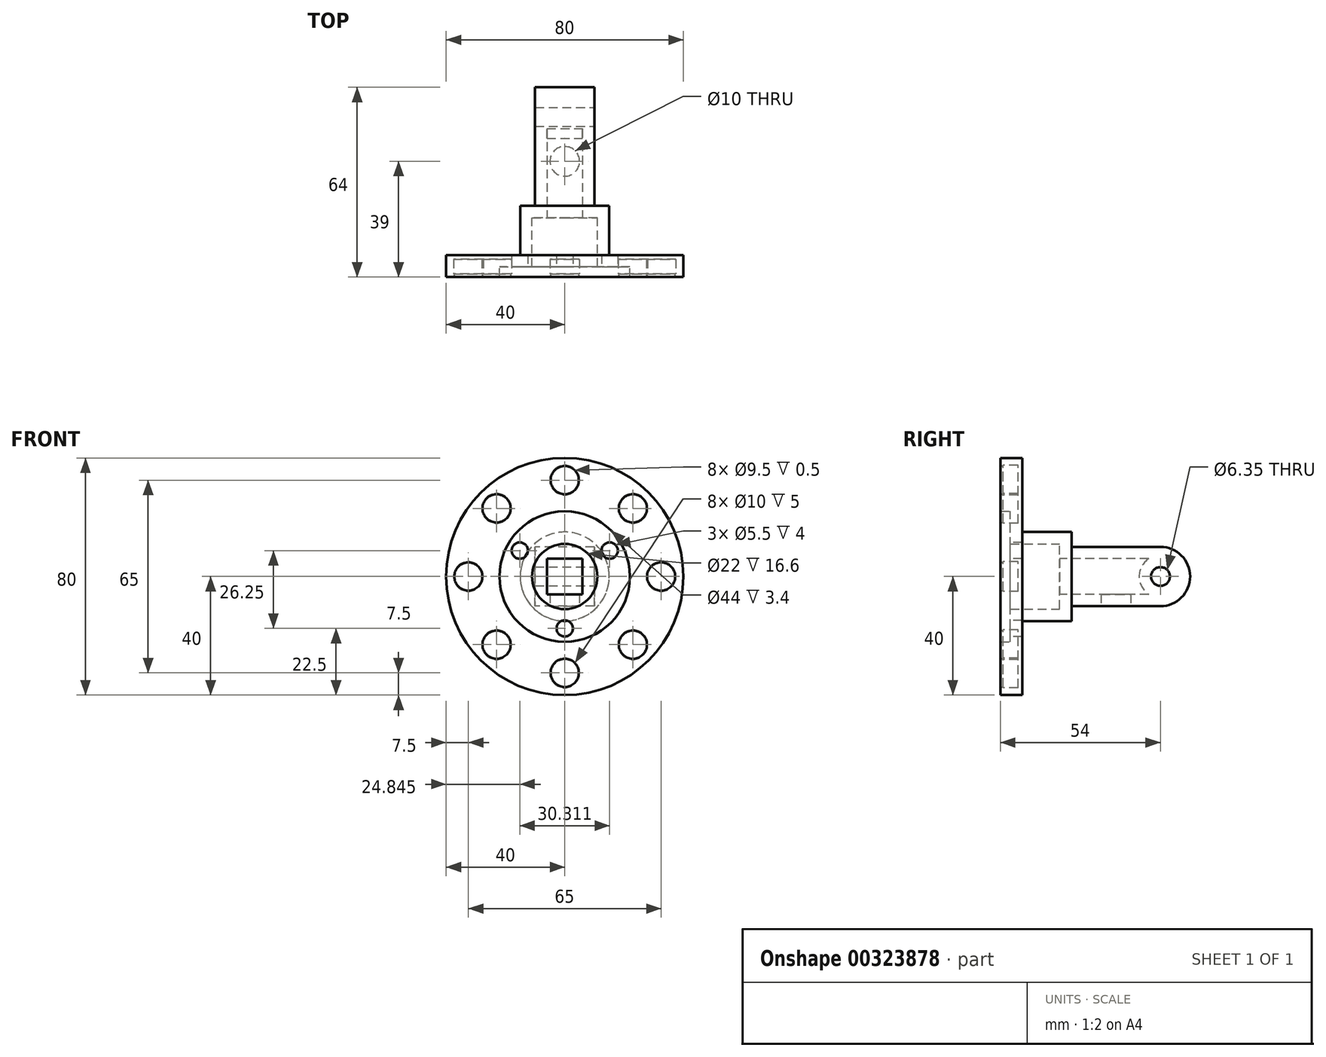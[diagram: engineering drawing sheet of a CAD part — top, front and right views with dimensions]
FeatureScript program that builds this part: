
annotation { "Feature Type Name" : "Feature", "Feature Type Description" : "" }
export const myFeature = defineFeature(function(context is Context, id is Id, definition is map)
    precondition{}
    {
        {
            var Q0;
            Q0=qCreatedBy(makeId("Top.planeOp"),FACE);
            var sketch = newSketch(context, id + "F0", { "sketchPlane" : qUnion([Q0])});
            skLineSegment(sketch, "E0.bottom", {"start": v(10, 15) * mm, "end": v(-10, 15) * mm});
            skLineSegment(sketch, "E0.top", {"start": v(10, -15) * mm, "end": v(-10, -15) * mm});
            skLineSegment(sketch, "E0.left", {"start": v(10, 15) * mm, "end": v(10, -15) * mm});
            skLineSegment(sketch, "E0.right", {"start": v(-10, 15) * mm, "end": v(-10, -15) * mm});
            skPoint(sketch, "E0.middle", {"position": v(0, 0) * mm});
            skSolve(sketch);
        }
        {
            var Q0;
            Q0=makeQuery(id+"F0.imprint","IMPRINT",FACE,{"disambiguationData":[TD([[makeQuery(id+"F0.imprint","IMPRINT",EDGE,{"derivedFrom":sQuery(id+"F0.wireOp",EDGE,"E0.bottom")}),1.0]])]});
            extrude(context, id + "F1", {"entities" : qUnion([Q0]), "depth" : 20 * mm});
        }
        {
            var Q0;
            Q0=makeQuery(id+"F1.opExtrude","CAP_EDGE",EDGE,{"disambiguationData":[OSD([sQuery(id+"F0.wireOp",EDGE,"E0.bottom")])],"isStart":false});
            var Q1;
            Q1=makeQuery(id+"F1.opExtrude","CAP_EDGE",EDGE,{"disambiguationData":[OSD([sQuery(id+"F0.wireOp",EDGE,"E0.bottom")])],"isStart":true});
            fillet(context, id + "F2", {"entities" : qUnion([Q0, Q1]), "radius" : 10 * mm, "tangentPropagation" : true, "allowEdgeOverflow" : false});
        }
        {
            var Q0;
            Q0=makeQuery(id+"F1.opExtrude","SWEPT_FACE",FACE,{"disambiguationData":[OSD([sQuery(id+"F0.wireOp",EDGE,"E0.left")])]});
            var sketch = newSketch(context, id + "F3", { "sketchPlane" : qUnion([Q0])});
            skCircle(sketch, "E1", {"center": v(5, 10) * mm, "radius": 3.18 * mm});
            skSolve(sketch);
        }
        {
            var Q0;
            Q0=makeQuery(id+"F3.imprint","IMPRINT",FACE,{"disambiguationData":[TD([[makeQuery(id+"F3.imprint","IMPRINT",EDGE,{"derivedFrom":sQuery(id+"F3.wireOp",EDGE,"E1")}),1.0]])]});
            extrude(context, id + "F4", {"entities" : qUnion([Q0]), "operationType" : NewBodyOperationType.REMOVE, "oppositeDirection" : true, "depth" : 25 * mm});
        }
        {
            var Q0;
            Q0=makeQuery(id+"F1.opExtrude","SWEPT_FACE",FACE,{"disambiguationData":[OSD([sQuery(id+"F0.wireOp",EDGE,"E0.top")])]});
            extrude(context, id + "F5", {"entities" : qUnion([Q0]), "operationType" : NewBodyOperationType.ADD, "depth" : 10 * mm});
        }
        {
            var Q0;
            Q0=makeQuery(id+"F5.opExtrude","CAP_FACE",FACE,{"disambiguationData":[OSD([sQuery(id+"F0.wireOp",EDGE,"E0.top")])],"isStart":false});
            shell(context, id + "F6", {"entities" : qUnion([Q0]), "thickness" : 4 * mm});
        }
        {
            var Q0;
            {var subQ0=sQuery(id+"F0.wireOp",EDGE,"E0.top");Q0=makeQuery(id+"F5.boolean.opBoolean","MERGE",FACE,{"derivedFrom":[makeQuery(id+"F1.opExtrude","CAP_FACE",FACE,{"disambiguationData":[OSD([sQuery(id+"F0.wireOp",EDGE,"E0.bottom"),subQ0,sQuery(id+"F0.wireOp",EDGE,"E0.left"),sQuery(id+"F0.wireOp",EDGE,"E0.right")])],"isStart":true}),makeQuery(id+"F5.opExtrude","SWEPT_FACE",FACE,{"disambiguationData":[OSD([subQ0]),TDD([makeQuery(id+"F1.opExtrude","CAP_EDGE",EDGE,{"disambiguationData":[OSD([subQ0])],"isStart":true})])]})]});}
            var sketch = newSketch(context, id + "F7", { "sketchPlane" : qUnion([Q0])});
            skCircle(sketch, "E2", {"center": v(0, 10) * mm, "radius": 5 * mm});
            skPoint(sketch, "E2.centerSnap0", {"position": v(0, 25) * mm});
            skSolve(sketch);
        }
        {
            var Q0;
            Q0=makeQuery(id+"F7.imprint","IMPRINT",FACE,{"disambiguationData":[TD([[makeQuery(id+"F7.imprint","IMPRINT",EDGE,{"derivedFrom":sQuery(id+"F7.wireOp",EDGE,"E2")}),1.0]])]});
            extrude(context, id + "F8", {"entities" : qUnion([Q0]), "operationType" : NewBodyOperationType.REMOVE, "oppositeDirection" : true, "depth" : 4 * mm});
        }
        {
            var Q0;
            Q0=makeQuery(id+"F5.opExtrude","CAP_FACE",FACE,{"disambiguationData":[OSD([sQuery(id+"F0.wireOp",EDGE,"E0.top")])],"isStart":false});
            var sketch = newSketch(context, id + "F9", { "sketchPlane" : qUnion([Q0])});
            skCircle(sketch, "E3", {"center": v(0, 10) * mm, "radius": 15 * mm});
            skPoint(sketch, "E3.centerSnap0", {"position": v(10, 10) * mm});
            skSolve(sketch);
        }
        {
            var Q0;
            Q0=makeQuery(id+"F9.imprint","IMPRINT",FACE,{"disambiguationData":[TD([[makeQuery(id+"F9.imprint","IMPRINT",EDGE,{"derivedFrom":sQuery(id+"F9.wireOp",EDGE,"E3")}),1.0]])]});
            var Q1;
            {var subQ0=sQuery(id+"F0.wireOp",EDGE,"E0.top");var subQ2=makeQuery(id+"F5.opExtrude","CAP_EDGE",EDGE,{"disambiguationData":[OSD([subQ0]),TDD([makeQuery(id+"F1.opExtrude","CAP_EDGE",EDGE,{"disambiguationData":[OSD([subQ0])],"isStart":true})])],"isStart":false});Q1=makeQuery(id+"F9.imprint","IMPRINT",FACE,{"disambiguationData":[TD([[makeQuery(id+"F9.imprint","IMPRINT",EDGE,{"derivedFrom":subQ2}),-1.0]])]});}
            extrude(context, id + "F10", {"entities" : qUnion([Q0, Q1]), "operationType" : NewBodyOperationType.ADD, "depth" : 4 * mm});
        }
        {
            var Q0;
            Q0=makeQuery(id+"F10.opExtrude","CAP_FACE",FACE,{"disambiguationData":[OSD([sQuery(id+"F0.wireOp",EDGE,"E0.top"),sQuery(id+"F0.wireOp",EDGE,"E0.left"),sQuery(id+"F0.wireOp",EDGE,"E0.right"),sQuery(id+"F9.wireOp",EDGE,"E3")])],"isStart":false});
            var sketch = newSketch(context, id + "F11", { "sketchPlane" : qUnion([Q0])});
            skCircle(sketch, "E4", {"center": v(0, 10) * mm, "radius": 11 * mm});
            skSolve(sketch);
        }
        {
            var Q0;
            Q0=makeQuery(id+"F11.imprint","IMPRINT",FACE,{"disambiguationData":[TD([[makeQuery(id+"F11.imprint","IMPRINT",EDGE,{"derivedFrom":sQuery(id+"F11.wireOp",EDGE,"E4")}),-1.0]])]});
            extrude(context, id + "F12", {"entities" : qUnion([Q0]), "operationType" : NewBodyOperationType.ADD, "depth" : 12.6 * mm});
        }
        {
            var Q0;
            Q0=makeQuery(id+"F12.opExtrude","CAP_FACE",FACE,{"disambiguationData":[OSD([sQuery(id+"F9.wireOp",EDGE,"E3"),sQuery(id+"F11.wireOp",EDGE,"E4")])],"isStart":false});
            var sketch = newSketch(context, id + "F13", { "sketchPlane" : qUnion([Q0])});
            skCircle(sketch, "E5", {"center": v(0, 10) * mm, "radius": 40 * mm});
            skSolve(sketch);
        }
        {
            var Q0;
            Q0=makeQuery(id+"F13.imprint","IMPRINT",FACE,{"disambiguationData":[TD([[makeQuery(id+"F13.imprint","IMPRINT",EDGE,{"derivedFrom":makeQuery(id+"F12.opExtrude","CAP_EDGE",EDGE,{"disambiguationData":[OSD([sQuery(id+"F11.wireOp",EDGE,"E4")])],"isStart":false})}),-1.0]])]});
            var Q1;
            Q1=makeQuery(id+"F13.imprint","IMPRINT",FACE,{"disambiguationData":[TD([[makeQuery(id+"F13.imprint","IMPRINT",EDGE,{"derivedFrom":sQuery(id+"F13.wireOp",EDGE,"E5")}),1.0]])]});
            extrude(context, id + "F14", {"entities" : qUnion([Q0, Q1]), "operationType" : NewBodyOperationType.ADD, "depth" : 4 * mm});
        }
        {
            var Q0;
            Q0=makeQuery(id+"F14.opExtrude","CAP_FACE",FACE,{"disambiguationData":[OSD([sQuery(id+"F11.wireOp",EDGE,"E4"),sQuery(id+"F13.wireOp",EDGE,"E5")])],"isStart":false});
            var sketch = newSketch(context, id + "F15", { "sketchPlane" : qUnion([Q0])});
            skCircle(sketch, "E6", {"center": v(0, 10) * mm, "radius": 22 * mm});
            skSolve(sketch);
        }
        {
            var Q0;
            Q0=makeQuery(id+"F15.imprint","IMPRINT",FACE,{"disambiguationData":[TD([[makeQuery(id+"F15.imprint","IMPRINT",EDGE,{"derivedFrom":sQuery(id+"F15.wireOp",EDGE,"E6")}),-1.0]])]});
            extrude(context, id + "F16", {"entities" : qUnion([Q0]), "operationType" : NewBodyOperationType.ADD, "depth" : 2.4 * mm});
        }
        {
            var Q0;
            Q0=makeQuery(id+"F14.opExtrude","CAP_FACE",FACE,{"disambiguationData":[OSD([sQuery(id+"F11.wireOp",EDGE,"E4"),sQuery(id+"F13.wireOp",EDGE,"E5")])],"isStart":false});
            var sketch = newSketch(context, id + "F17", { "sketchPlane" : qUnion([Q0])});
            skCircle(sketch, "E7", {"center": v(0, -7.5) * mm, "radius": 2.75 * mm});
            skCircle(sketch, "E8.1.0", {"center": v(15.16, 18.75) * mm, "radius": 2.75 * mm});
            skCircle(sketch, "E8.2.0", {"center": v(-15.16, 18.75) * mm, "radius": 2.75 * mm});
            skPoint(sketch, "E8.center", {"position": v(0, 10) * mm});
            skSolve(sketch);
        }
        {
            var Q0;
            Q0=makeQuery(id+"F17.imprint","IMPRINT",FACE,{"disambiguationData":[TD([[makeQuery(id+"F17.imprint","IMPRINT",EDGE,{"derivedFrom":sQuery(id+"F17.wireOp",EDGE,"E8.1.0")}),1.0]])]});
            var Q1;
            Q1=makeQuery(id+"F17.imprint","IMPRINT",FACE,{"disambiguationData":[TD([[makeQuery(id+"F17.imprint","IMPRINT",EDGE,{"derivedFrom":sQuery(id+"F17.wireOp",EDGE,"E7")}),1.0]])]});
            var Q2;
            Q2=makeQuery(id+"F17.imprint","IMPRINT",FACE,{"disambiguationData":[TD([[makeQuery(id+"F17.imprint","IMPRINT",EDGE,{"derivedFrom":sQuery(id+"F17.wireOp",EDGE,"E8.2.0")}),1.0]])]});
            extrude(context, id + "F18", {"entities" : qUnion([Q0, Q1, Q2]), "operationType" : NewBodyOperationType.REMOVE, "oppositeDirection" : true, "depth" : 4 * mm});
        }
        {
            var Q0;
            Q0=makeQuery(id+"F16.opExtrude","CAP_FACE",FACE,{"disambiguationData":[OSD([sQuery(id+"F13.wireOp",EDGE,"E5"),sQuery(id+"F15.wireOp",EDGE,"E6")])],"isStart":false});
            var sketch = newSketch(context, id + "F19", { "sketchPlane" : qUnion([Q0])});
            skCircle(sketch, "E9", {"center": v(0, -22.5) * mm, "radius": 5 * mm});
            skCircle(sketch, "E10.1.0", {"center": v(22.98, -12.98) * mm, "radius": 5 * mm});
            skCircle(sketch, "E10.2.0", {"center": v(32.5, 10) * mm, "radius": 5 * mm});
            skCircle(sketch, "E10.3.0", {"center": v(22.98, 32.98) * mm, "radius": 5 * mm});
            skCircle(sketch, "E10.4.0", {"center": v(0, 42.5) * mm, "radius": 5 * mm});
            skCircle(sketch, "E10.5.0", {"center": v(-22.98, 32.98) * mm, "radius": 5 * mm});
            skCircle(sketch, "E10.6.0", {"center": v(-32.5, 10) * mm, "radius": 5 * mm});
            skCircle(sketch, "E10.7.0", {"center": v(-22.98, -12.98) * mm, "radius": 5 * mm});
            skPoint(sketch, "E10.center", {"position": v(0, 10) * mm});
            skSolve(sketch);
        }
        {
            var Q0;
            Q0=makeQuery(id+"F19.imprint","IMPRINT",FACE,{"disambiguationData":[TD([[makeQuery(id+"F19.imprint","IMPRINT",EDGE,{"derivedFrom":sQuery(id+"F19.wireOp",EDGE,"E10.4.0")}),1.0]])]});
            var Q1;
            Q1=makeQuery(id+"F19.imprint","IMPRINT",FACE,{"disambiguationData":[TD([[makeQuery(id+"F19.imprint","IMPRINT",EDGE,{"derivedFrom":sQuery(id+"F19.wireOp",EDGE,"E10.5.0")}),1.0]])]});
            var Q2;
            Q2=makeQuery(id+"F19.imprint","IMPRINT",FACE,{"disambiguationData":[TD([[makeQuery(id+"F19.imprint","IMPRINT",EDGE,{"derivedFrom":sQuery(id+"F19.wireOp",EDGE,"E10.6.0")}),1.0]])]});
            var Q3;
            Q3=makeQuery(id+"F19.imprint","IMPRINT",FACE,{"disambiguationData":[TD([[makeQuery(id+"F19.imprint","IMPRINT",EDGE,{"derivedFrom":sQuery(id+"F19.wireOp",EDGE,"E10.7.0")}),1.0]])]});
            var Q4;
            Q4=makeQuery(id+"F19.imprint","IMPRINT",FACE,{"disambiguationData":[TD([[makeQuery(id+"F19.imprint","IMPRINT",EDGE,{"derivedFrom":sQuery(id+"F19.wireOp",EDGE,"E9")}),1.0]])]});
            var Q5;
            Q5=makeQuery(id+"F19.imprint","IMPRINT",FACE,{"disambiguationData":[TD([[makeQuery(id+"F19.imprint","IMPRINT",EDGE,{"derivedFrom":sQuery(id+"F19.wireOp",EDGE,"E10.1.0")}),1.0]])]});
            var Q6;
            Q6=makeQuery(id+"F19.imprint","IMPRINT",FACE,{"disambiguationData":[TD([[makeQuery(id+"F19.imprint","IMPRINT",EDGE,{"derivedFrom":sQuery(id+"F19.wireOp",EDGE,"E10.2.0")}),1.0]])]});
            var Q7;
            Q7=makeQuery(id+"F19.imprint","IMPRINT",FACE,{"disambiguationData":[TD([[makeQuery(id+"F19.imprint","IMPRINT",EDGE,{"derivedFrom":sQuery(id+"F19.wireOp",EDGE,"E10.3.0")}),1.0]])]});
            extrude(context, id + "F20", {"entities" : qUnion([Q0, Q1, Q2, Q3, Q4, Q5, Q6, Q7]), "operationType" : NewBodyOperationType.REMOVE, "oppositeDirection" : true, "depth" : 5 * mm});
        }
        {
            var Q0;
            Q0=makeQuery(id+"F16.opExtrude","CAP_FACE",FACE,{"disambiguationData":[OSD([sQuery(id+"F13.wireOp",EDGE,"E5"),sQuery(id+"F15.wireOp",EDGE,"E6")])],"isStart":false});
            var sketch = newSketch(context, id + "F21", { "sketchPlane" : qUnion([Q0])});
            skCircle(sketch, "E11", {"center": v(0, 10) * mm, "radius": 40 * mm});
            skCircle(sketch, "E12", {"center": v(0, 42.5) * mm, "radius": 4.75 * mm});
            skCircle(sketch, "E13.1.0", {"center": v(-22.98, 32.98) * mm, "radius": 4.75 * mm});
            skCircle(sketch, "E13.2.0", {"center": v(-32.5, 10) * mm, "radius": 4.75 * mm});
            skCircle(sketch, "E13.3.0", {"center": v(-22.98, -12.98) * mm, "radius": 4.75 * mm});
            skCircle(sketch, "E13.4.0", {"center": v(0, -22.5) * mm, "radius": 4.75 * mm});
            skCircle(sketch, "E13.5.0", {"center": v(22.98, -12.98) * mm, "radius": 4.75 * mm});
            skCircle(sketch, "E13.6.0", {"center": v(32.5, 10) * mm, "radius": 4.75 * mm});
            skCircle(sketch, "E13.7.0", {"center": v(22.98, 32.98) * mm, "radius": 4.75 * mm});
            skSolve(sketch);
        }
        {
            var Q0;
            Q0=makeQuery(id+"F21.imprint","IMPRINT",FACE,{"disambiguationData":[TD([[makeQuery(id+"F21.imprint","IMPRINT",EDGE,{"derivedFrom":sQuery(id+"F21.wireOp",EDGE,"E11")}),1.0]])]});
            var Q1;
            Q1=makeQuery(id+"F21.imprint","IMPRINT",FACE,{"disambiguationData":[TD([[makeQuery(id+"F21.imprint","IMPRINT",EDGE,{"derivedFrom":sQuery(id+"F21.wireOp",EDGE,"E12")}),-1.0]])]});
            var Q2;
            Q2=makeQuery(id+"F21.imprint","IMPRINT",FACE,{"disambiguationData":[TD([[makeQuery(id+"F21.imprint","IMPRINT",EDGE,{"derivedFrom":sQuery(id+"F21.wireOp",EDGE,"E13.7.0")}),-1.0]])]});
            var Q3;
            Q3=makeQuery(id+"F21.imprint","IMPRINT",FACE,{"disambiguationData":[TD([[makeQuery(id+"F21.imprint","IMPRINT",EDGE,{"derivedFrom":sQuery(id+"F21.wireOp",EDGE,"E13.1.0")}),-1.0]])]});
            var Q4;
            Q4=makeQuery(id+"F21.imprint","IMPRINT",FACE,{"disambiguationData":[TD([[makeQuery(id+"F21.imprint","IMPRINT",EDGE,{"derivedFrom":sQuery(id+"F21.wireOp",EDGE,"E13.6.0")}),-1.0]])]});
            var Q5;
            Q5=makeQuery(id+"F21.imprint","IMPRINT",FACE,{"disambiguationData":[TD([[makeQuery(id+"F21.imprint","IMPRINT",EDGE,{"derivedFrom":sQuery(id+"F21.wireOp",EDGE,"E13.2.0")}),-1.0]])]});
            var Q6;
            Q6=makeQuery(id+"F21.imprint","IMPRINT",FACE,{"disambiguationData":[TD([[makeQuery(id+"F21.imprint","IMPRINT",EDGE,{"derivedFrom":sQuery(id+"F21.wireOp",EDGE,"E13.3.0")}),-1.0]])]});
            var Q7;
            Q7=makeQuery(id+"F21.imprint","IMPRINT",FACE,{"disambiguationData":[TD([[makeQuery(id+"F21.imprint","IMPRINT",EDGE,{"derivedFrom":sQuery(id+"F21.wireOp",EDGE,"E13.4.0")}),-1.0]])]});
            var Q8;
            Q8=makeQuery(id+"F21.imprint","IMPRINT",FACE,{"disambiguationData":[TD([[makeQuery(id+"F21.imprint","IMPRINT",EDGE,{"derivedFrom":sQuery(id+"F21.wireOp",EDGE,"E13.5.0")}),-1.0]])]});
            extrude(context, id + "F22", {"entities" : qUnion([Q0, Q1, Q2, Q3, Q4, Q5, Q6, Q7, Q8]), "operationType" : NewBodyOperationType.ADD, "depth" : 1 * mm});
        }
        {
            var Q0;
            Q0=makeQuery(id+"F22.opExtrude","CAP_EDGE",EDGE,{"disambiguationData":[OSD([sQuery(id+"F21.wireOp",EDGE,"E12")])],"isStart":false});
            var Q1;
            Q1=makeQuery(id+"F22.opExtrude","CAP_EDGE",EDGE,{"disambiguationData":[OSD([sQuery(id+"F21.wireOp",EDGE,"E13.7.0")])],"isStart":false});
            var Q2;
            Q2=makeQuery(id+"F22.opExtrude","CAP_EDGE",EDGE,{"disambiguationData":[OSD([sQuery(id+"F21.wireOp",EDGE,"E13.6.0")])],"isStart":false});
            var Q3;
            Q3=makeQuery(id+"F22.opExtrude","CAP_EDGE",EDGE,{"disambiguationData":[OSD([sQuery(id+"F21.wireOp",EDGE,"E13.1.0")])],"isStart":false});
            var Q4;
            Q4=makeQuery(id+"F22.opExtrude","CAP_EDGE",EDGE,{"disambiguationData":[OSD([sQuery(id+"F21.wireOp",EDGE,"E13.2.0")])],"isStart":false});
            var Q5;
            Q5=makeQuery(id+"F22.opExtrude","CAP_EDGE",EDGE,{"disambiguationData":[OSD([sQuery(id+"F21.wireOp",EDGE,"E13.3.0")])],"isStart":false});
            var Q6;
            Q6=makeQuery(id+"F22.opExtrude","CAP_EDGE",EDGE,{"disambiguationData":[OSD([sQuery(id+"F21.wireOp",EDGE,"E13.4.0")])],"isStart":false});
            var Q7;
            Q7=makeQuery(id+"F22.opExtrude","CAP_EDGE",EDGE,{"disambiguationData":[OSD([sQuery(id+"F21.wireOp",EDGE,"E13.5.0")])],"isStart":false});
            fillet(context, id + "F23", {"entities" : qUnion([Q0, Q1, Q2, Q3, Q4, Q5, Q6, Q7]), "radius" : .5 * mm, "tangentPropagation" : true, "allowEdgeOverflow" : false});
        }
    });
